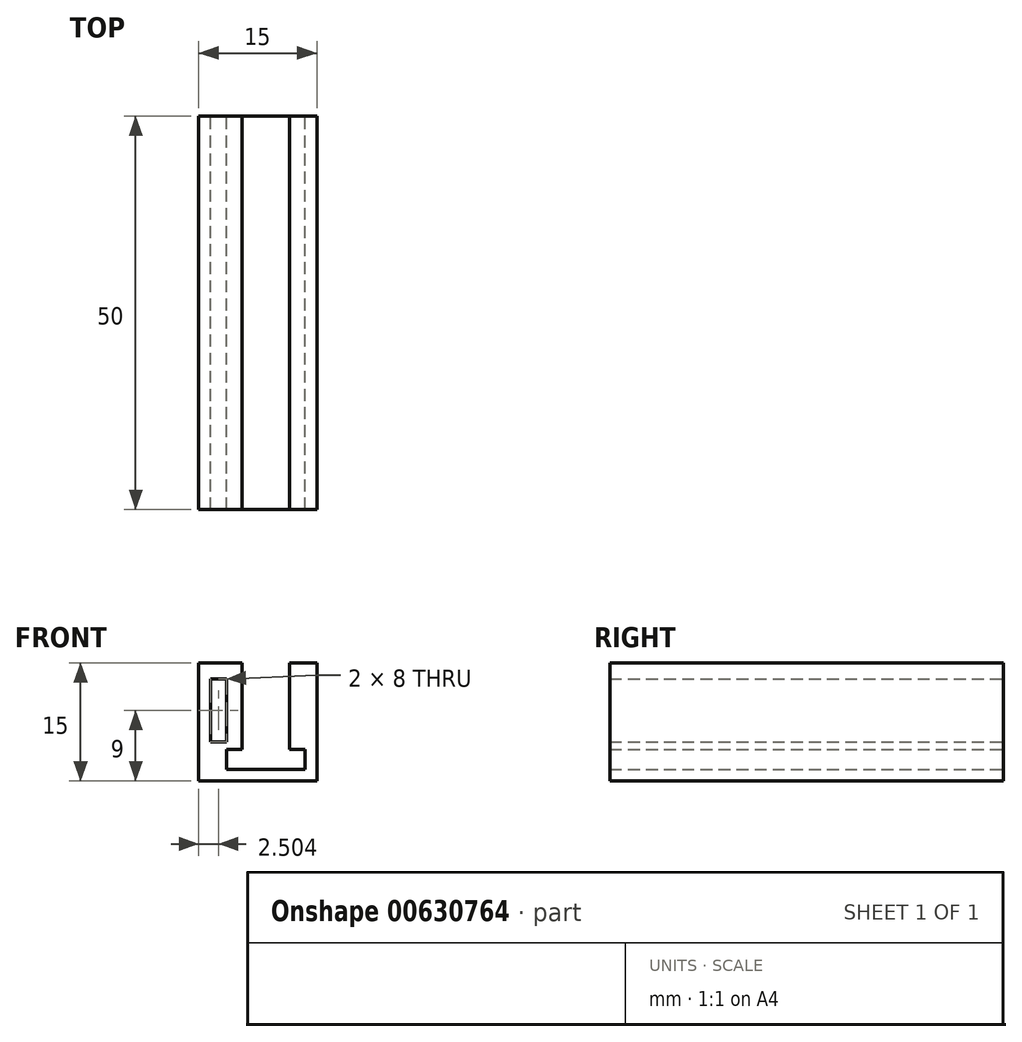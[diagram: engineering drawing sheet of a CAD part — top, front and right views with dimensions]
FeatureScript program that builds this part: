
annotation { "Feature Type Name" : "Feature", "Feature Type Description" : "" }
export const myFeature = defineFeature(function(context is Context, id is Id, definition is map)
    precondition{}
    {
        {
            var Q0;
            Q0=qCreatedBy(makeId("Front.planeOp"),FACE);
            var sketch = newSketch(context, id + "F0", { "sketchPlane" : qUnion([Q0])});
            skLineSegment(sketch, "E0.bottom", {"start": v(-26.49, 9.5) * mm, "end": v(-11.49, 9.5) * mm});
            skLineSegment(sketch, "E0.top", {"start": v(-26.49, -5.5) * mm, "end": v(-11.49, -5.5) * mm});
            skLineSegment(sketch, "E0.left", {"start": v(-26.49, 9.5) * mm, "end": v(-26.49, -5.5) * mm});
            skLineSegment(sketch, "E0.right", {"start": v(-11.49, 9.5) * mm, "end": v(-11.49, -5.5) * mm});
            skLineSegment(sketch, "E1.bottom", {"start": v(-24.99, 7.5) * mm, "end": v(-22.99, 7.5) * mm});
            skLineSegment(sketch, "E1.top", {"start": v(-24.99, -0.5) * mm, "end": v(-22.99, -0.5) * mm});
            skLineSegment(sketch, "E1.left", {"start": v(-24.99, 7.5) * mm, "end": v(-24.99, -0.5) * mm});
            skLineSegment(sketch, "E1.right", {"start": v(-22.99, 7.5) * mm, "end": v(-22.99, -0.5) * mm});
            skLineSegment(sketch, "E2.bottom", {"start": v(-22.99, -1.5) * mm, "end": v(-12.99, -1.5) * mm});
            skLineSegment(sketch, "E2.top", {"start": v(-22.99, -4) * mm, "end": v(-12.99, -4) * mm});
            skLineSegment(sketch, "E2.left", {"start": v(-22.99, -1.5) * mm, "end": v(-22.99, -4) * mm});
            skLineSegment(sketch, "E2.right", {"start": v(-12.99, -1.5) * mm, "end": v(-12.99, -4) * mm});
            skLineSegment(sketch, "E3.left", {"start": v(-22.99, 5) * mm, "end": v(-22.99, 0) * mm});
            skLineSegment(sketch, "E4.bottom", {"start": v(-20.99, 9.52) * mm, "end": v(-14.99, 9.52) * mm});
            skLineSegment(sketch, "E4.top", {"start": v(-20.99, -2.1) * mm, "end": v(-14.99, -2.1) * mm});
            skLineSegment(sketch, "E4.left", {"start": v(-20.99, 9.52) * mm, "end": v(-20.99, -2.1) * mm});
            skLineSegment(sketch, "E4.right", {"start": v(-14.99, 9.52) * mm, "end": v(-14.99, -2.1) * mm});
            skSolve(sketch);
        }
        {
            var Q0;
            {var subQ6=sQuery(id+"F0.wireOp",EDGE,"E0.bottom");Q0=makeQuery(id+"F0.imprint","IMPRINT",FACE,{"disambiguationData":[TD([[makeQuery(id+"F0.imprint","IMPRINT",EDGE,{"derivedFrom":subQ6}),-1.0]])]});}
            extrude(context, id + "F1", {"entities" : qUnion([Q0]), "depth" : 50 * mm, "offsetDistance" : 25 * mm});
        }
    });
